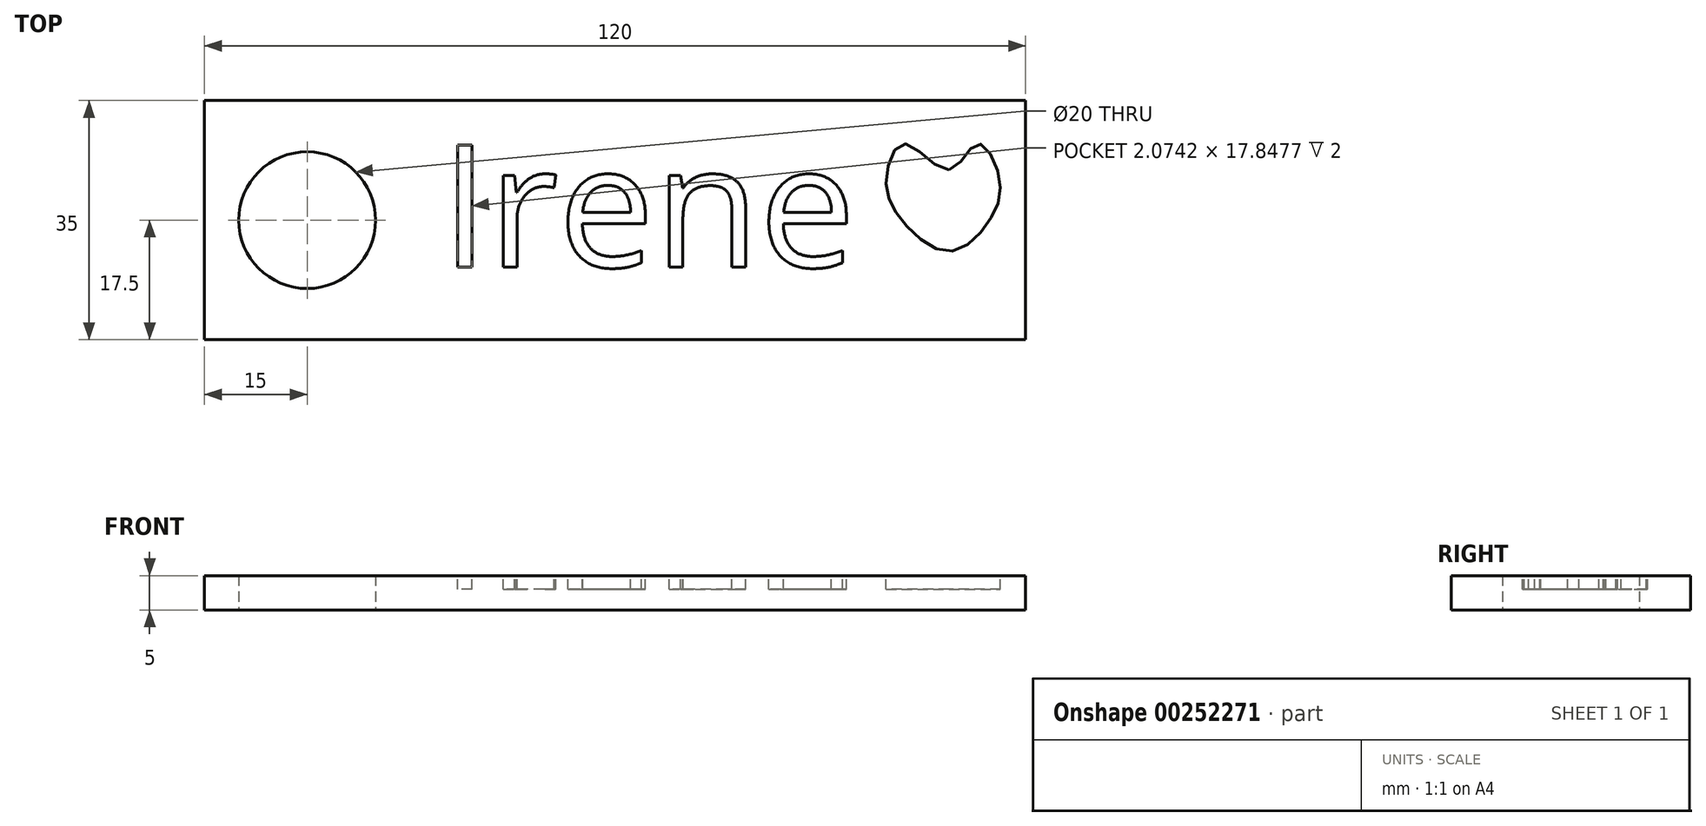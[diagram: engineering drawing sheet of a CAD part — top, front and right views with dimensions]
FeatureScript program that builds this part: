
annotation { "Feature Type Name" : "Feature", "Feature Type Description" : "" }
export const myFeature = defineFeature(function(context is Context, id is Id, definition is map)
    precondition{}
    {
        {
            var Q0;
            Q0=qCreatedBy(makeId("Top.planeOp"),FACE);
            var sketch = newSketch(context, id + "F0", { "sketchPlane" : qUnion([Q0])});
            skLineSegment(sketch, "E0.bottom", {"start": v(60, 17.5) * mm, "end": v(-60, 17.5) * mm});
            skLineSegment(sketch, "E0.top", {"start": v(60, -17.5) * mm, "end": v(-60, -17.5) * mm});
            skLineSegment(sketch, "E0.left", {"start": v(60, 17.5) * mm, "end": v(60, -17.5) * mm});
            skLineSegment(sketch, "E0.right", {"start": v(-60, 17.5) * mm, "end": v(-60, -17.5) * mm});
            skPoint(sketch, "E0.middle", {"position": v(0, 0) * mm});
            skCircle(sketch, "E1", {"center": v(-45, 0) * mm, "radius": 10 * mm});
            skSolve(sketch);
        }
        {
            var Q0;
            Q0=makeQuery(id+"F0.imprint","IMPRINT",FACE,{"disambiguationData":[TD([[makeQuery(id+"F0.imprint","IMPRINT",EDGE,{"derivedFrom":sQuery(id+"F0.wireOp",EDGE,"E0.bottom")}),1.0]])]});
            extrude(context, id + "F1", {"entities" : qUnion([Q0]), "depth" : 5 * mm});
        }
        {
            var Q0;
            Q0=makeQuery(id+"F1.opExtrude","CAP_FACE",FACE,{"disambiguationData":[OSD([sQuery(id+"F0.wireOp",EDGE,"E0.bottom"),sQuery(id+"F0.wireOp",EDGE,"E0.top"),sQuery(id+"F0.wireOp",EDGE,"E0.left"),sQuery(id+"F0.wireOp",EDGE,"E0.right"),sQuery(id+"F0.wireOp",EDGE,"E1")])],"isStart":false});
            var sketch = newSketch(context, id + "F2", { "sketchPlane" : qUnion([Q0])});
            skText(sketch, "E2", { "text": "Irene\n", "fontName": "OpenSans-Regular.ttf"});
            skFitSpline(sketch, "E3", {"points": [v(48.8, 7.34) * mm, v(42.38, 11.15) * mm, v(39.63, 5.96) * mm, v(41.92, 0) * mm, v(48.8, -4.59) * mm, v(54.76, 0) * mm, v(56.14, 6.42) * mm, v(52.93, 11.15) * mm, v(48.8, 7.34) * mm]});
            const initialGuessF2  = {"E2": [-0.02546, -0.00685, 1, 0, 0.018]};
            skSetInitialGuess(sketch, initialGuessF2);
            skSolve(sketch);
        }
        {
            var Q0;
            Q0 = qSketchRegion(id + "F2", true);
            extrude(context, id + "F3", {"entities" : qUnion([Q0]), "operationType" : NewBodyOperationType.REMOVE, "oppositeDirection" : true, "depth" : 2 * mm});
        }
    });
